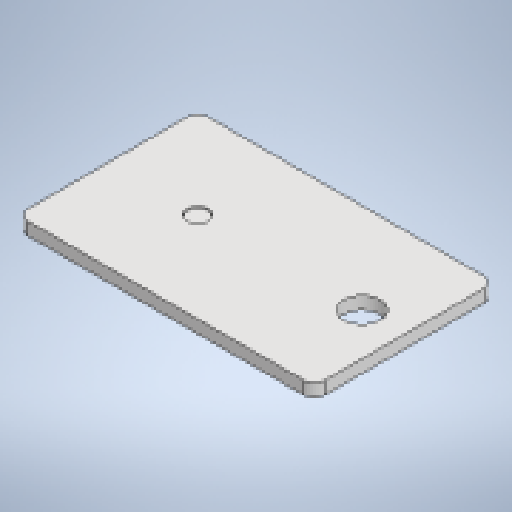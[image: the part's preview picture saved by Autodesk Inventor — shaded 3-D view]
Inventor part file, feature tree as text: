
AUTODESK INVENTOR PART (.ipt)
format: ipt  version: 2025.1 (Build 291241020, 241B)  size: 185,856 bytes
history: native  units: mm
features: sketch x2, other x2, sheet_metal_op x1, extrude x1, chamfer x1
ambient origin geometry x8: Origin, YZ Plane, XZ Plane, XY Plane, X Axis, Y Axis, Z Axis, Center Point
bodies: Solid1 (feature_tree)
feature tree (7):
  sheet_metal_op  "Face1"
  extrude  "Extrusion2"  Depth=85.0mm
  chamfer  "Corner Round2"
  sketch  "Sketch1"  dims[d0=150.0mm d1=85.0mm]
  other  "Plate1"
  sketch  "Sketch5"  dims[d2=6.0mm d23=17.0mm d25=20.0mm d26=20.0mm d27=10.0mm d28=1.0mm d29=0.0mm d33=5.0mm]
  other  "Definition1"
